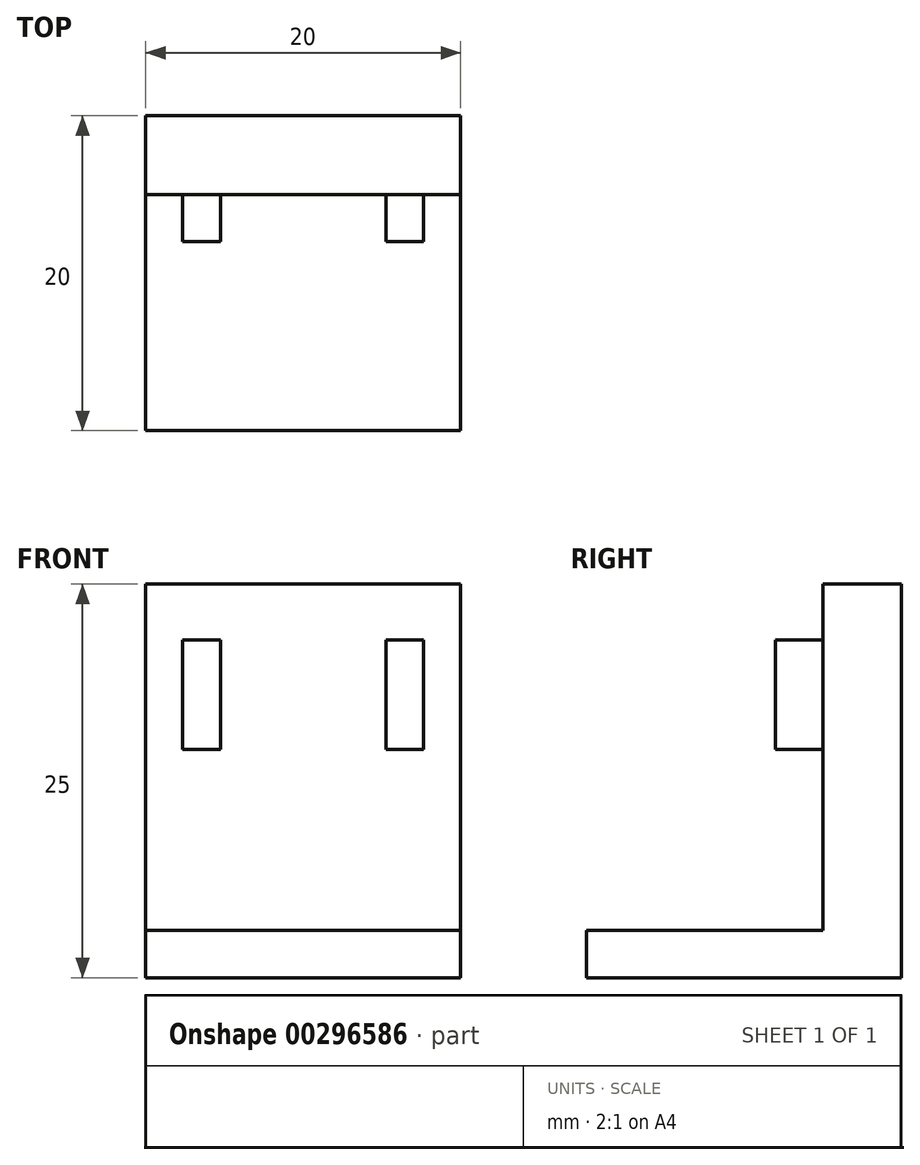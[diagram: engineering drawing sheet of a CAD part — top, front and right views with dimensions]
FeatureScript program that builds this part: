
annotation { "Feature Type Name" : "Feature", "Feature Type Description" : "" }
export const myFeature = defineFeature(function(context is Context, id is Id, definition is map)
    precondition{}
    {
        {
            var Q0;
            Q0=qCreatedBy(makeId("Front.planeOp"),FACE);
            var sketch = newSketch(context, id + "F0", { "sketchPlane" : qUnion([Q0])});
            skLineSegment(sketch, "E0.bottom", {"start": v(0, 0) * mm, "end": v(20, 0) * mm});
            skLineSegment(sketch, "E0.top", {"start": v(0, 25) * mm, "end": v(20, 25) * mm});
            skLineSegment(sketch, "E0.left", {"start": v(0, 0) * mm, "end": v(0, 25) * mm});
            skLineSegment(sketch, "E0.right", {"start": v(20, 0) * mm, "end": v(20, 25) * mm});
            skSolve(sketch);
        }
        {
            var Q0;
            Q0 = qSketchRegion(id + "F0", true);
            extrude(context, id + "F1", {"entities" : qUnion([Q0]), "depth" : 5 * mm});
        }
        {
            var Q0;
            Q0=makeQuery(id+"F1.opExtrude","CAP_FACE",FACE,{"disambiguationData":[OSD([sQuery(id+"F0.wireOp",EDGE,"E0.bottom"),sQuery(id+"F0.wireOp",EDGE,"E0.top"),sQuery(id+"F0.wireOp",EDGE,"E0.left"),sQuery(id+"F0.wireOp",EDGE,"E0.right")])],"isStart":false});
            var sketch = newSketch(context, id + "F2", { "sketchPlane" : qUnion([Q0])});
            skLineSegment(sketch, "E1.bottom", {"start": v(0, 0) * mm, "end": v(20, 0) * mm});
            skLineSegment(sketch, "E1.top", {"start": v(0, 3) * mm, "end": v(20, 3) * mm});
            skLineSegment(sketch, "E1.left", {"start": v(0, 0) * mm, "end": v(0, 3) * mm});
            skLineSegment(sketch, "E1.right", {"start": v(20, 0) * mm, "end": v(20, 3) * mm});
            skSolve(sketch);
        }
        {
            var Q0;
            Q0 = qSketchRegion(id + "F2", true);
            extrude(context, id + "F3", {"entities" : qUnion([Q0]), "operationType" : NewBodyOperationType.ADD, "depth" : 15 * mm});
        }
        {
            var Q0;
            Q0=makeQuery(id+"F1.opExtrude","CAP_FACE",FACE,{"disambiguationData":[OSD([sQuery(id+"F0.wireOp",EDGE,"E0.bottom"),sQuery(id+"F0.wireOp",EDGE,"E0.top"),sQuery(id+"F0.wireOp",EDGE,"E0.left"),sQuery(id+"F0.wireOp",EDGE,"E0.right")])],"isStart":false});
            var sketch = newSketch(context, id + "F4", { "sketchPlane" : qUnion([Q0])});
            skLineSegment(sketch, "E2.bottom", {"start": v(2.35, 21.46) * mm, "end": v(4.75, 21.46) * mm});
            skLineSegment(sketch, "E2.top", {"start": v(2.35, 14.5) * mm, "end": v(4.75, 14.5) * mm});
            skLineSegment(sketch, "E2.left", {"start": v(2.35, 21.46) * mm, "end": v(2.35, 14.5) * mm});
            skLineSegment(sketch, "E2.right", {"start": v(4.75, 21.46) * mm, "end": v(4.75, 14.5) * mm});
            skLineSegment(sketch, "E3.bottom", {"start": v(15.25, 21.46) * mm, "end": v(17.65, 21.46) * mm});
            skLineSegment(sketch, "E3.top", {"start": v(15.25, 14.5) * mm, "end": v(17.65, 14.5) * mm});
            skLineSegment(sketch, "E3.left", {"start": v(15.25, 21.46) * mm, "end": v(15.25, 14.5) * mm});
            skLineSegment(sketch, "E3.right", {"start": v(17.65, 21.46) * mm, "end": v(17.65, 14.5) * mm});
            skLineSegment(sketch, "E4", {"start": v(0, 14.5) * mm, "end": v(2.35, 14.5) * mm, "construction": true});
            skLineSegment(sketch, "E5", {"start": v(17.65, 14.5) * mm, "end": v(20, 14.5) * mm, "construction": true});
            skLineSegment(sketch, "E6", {"start": v(4.75, 21.46) * mm, "end": v(15.25, 21.46) * mm, "construction": true});
            skLineSegment(sketch, "E7", {"start": v(2.35, 14.5) * mm, "end": v(2.35, 3) * mm, "construction": true});
            skSolve(sketch);
        }
        {
            var Q0;
            Q0 = qSketchRegion(id + "F4", true);
            extrude(context, id + "F5", {"entities" : qUnion([Q0]), "operationType" : NewBodyOperationType.ADD, "depth" : 3 * mm});
        }
    });
